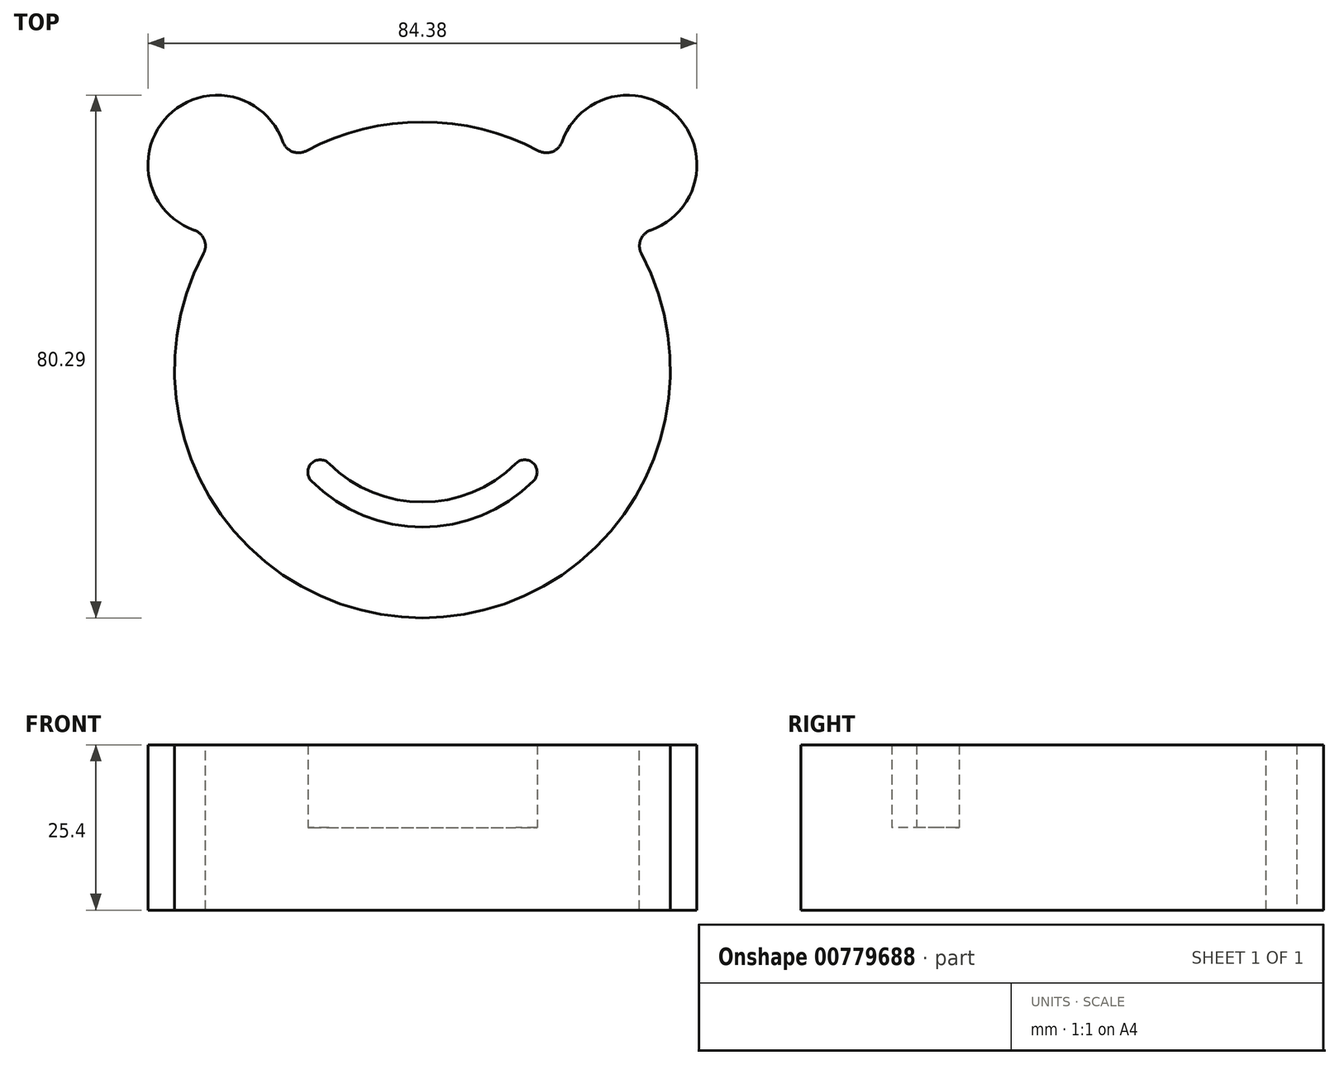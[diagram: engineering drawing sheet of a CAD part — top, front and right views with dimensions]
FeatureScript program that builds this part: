
annotation { "Feature Type Name" : "Feature", "Feature Type Description" : "" }
export const myFeature = defineFeature(function(context is Context, id is Id, definition is map)
    precondition{}
    {
        {
            var Q0;
            Q0=qCreatedBy(makeId("Top.planeOp"),FACE);
            var sketch = newSketch(context, id + "F0", { "sketchPlane" : qUnion([Q0])});
            skCircle(sketch, "E0", {"center": v(0, 0) * mm, "radius": 38.1 * mm});
            skCircle(sketch, "E1", {"center": v(0, 0) * mm, "radius": 31.75 * mm});
            skLineSegment(sketch, "E2", {"start": v(0, 31.75) * mm, "end": v(0, 55.25) * mm, "construction": true});
            skLineSegment(sketch, "E3", {"start": v(0, 55.25) * mm, "end": v(0, 44.58) * mm, "construction": true});
            skArc(sketch, "E4", {"start": v(7.8, 37.3) * mm, "mid": v(0, 55.25) * mm, "end": v(-7.8, 37.3) * mm});
            skArc(sketch, "E5.1.0", {"start": v(37.3, -7.8) * mm, "mid": v(55.25, 0) * mm, "end": v(37.3, 7.8) * mm});
            skLineSegment(sketch, "E5.anchor1", {"start": v(0, 0) * mm, "end": v(-7.8, 37.3) * mm, "construction": true});
            skLineSegment(sketch, "E5.anchor2", {"start": v(0, 0) * mm, "end": v(37.3, 7.8) * mm, "construction": true});
            skSolve(sketch);
        }
        {
            var Q0;
            Q0=qCreatedBy(makeId("Front.planeOp"),FACE);
            var sketch = newSketch(context, id + "F1", { "sketchPlane" : qUnion([Q0])});
            skLineSegment(sketch, "E6", {"start": v(0, 0) * mm, "end": v(0, 59.39) * mm, "construction": true});
            skSolve(sketch);
        }
        {
            var Q0;
            Q0 = qSketchRegion(id + "F0", true);
            var Q1;
            Q1=makeQuery(id+"F0.imprint","IMPRINT",FACE,{"disambiguationData":[TD([[makeQuery(id+"F0.imprint","IMPRINT",EDGE,{"derivedFrom":sQuery(id+"F0.wireOp",EDGE,"E1")}),1.0]])]});
            extrude(context, id + "F2", {"entities" : qUnion([Q0, Q1]), "depth" : 12.7 * mm, "offsetDistance" : 25.4 * mm});
        }
        {
            var Q0;
            Q0=makeQuery(id+"F2.opExtrude","CAP_FACE",FACE,{"disambiguationData":[OSD([sQuery(id+"F0.wireOp",EDGE,"E0"),sQuery(id+"F0.wireOp",EDGE,"E4"),sQuery(id+"F0.wireOp",EDGE,"E5.1.0")])],"isStart":false});
            var sketch = newSketch(context, id + "F3", { "sketchPlane" : qUnion([Q0])});
            skCircle(sketch, "E7", {"center": v(0, 20.32) * mm, "radius": 5.08 * mm});
            skCircle(sketch, "E8", {"center": v(20.32, 0) * mm, "radius": 5.08 * mm});
            skArc(sketch, "E9", {"start": v(0, -20.32) * mm, "mid": v(-14.37, -14.37) * mm, "end": v(-20.32, 0) * mm});
            skArc(sketch, "E10", {"start": v(0, -24.13) * mm, "mid": v(-17.06, -17.06) * mm, "end": v(-24.13, 0) * mm});
            skArc(sketch, "E11", {"start": v(-24.13, 0) * mm, "mid": v(-22.23, 1.9) * mm, "end": v(-20.32, 0) * mm});
            skArc(sketch, "E12", {"start": v(0, -24.13) * mm, "mid": v(1.9, -22.23) * mm, "end": v(0, -20.32) * mm});
            skSolve(sketch);
        }
        {
            var Q0;
            Q0=makeQuery(id+"F3.imprint","IMPRINT",FACE,{"disambiguationData":[TD([[makeQuery(id+"F3.imprint","IMPRINT",EDGE,{"derivedFrom":sQuery(id+"F3.wireOp",EDGE,"E7")}),1.0]])]});
            var Q1;
            Q1=makeQuery(id+"F3.imprint","IMPRINT",FACE,{"disambiguationData":[TD([[makeQuery(id+"F3.imprint","IMPRINT",EDGE,{"derivedFrom":sQuery(id+"F3.wireOp",EDGE,"E8")}),1.0]])]});
            var Q2;
            Q2=makeQuery(id+"F3.imprint","IMPRINT",FACE,{"disambiguationData":[TD([[makeQuery(id+"F3.imprint","IMPRINT",EDGE,{"derivedFrom":sQuery(id+"F3.wireOp",EDGE,"E9")}),1.0]])]});
            extrude(context, id + "F4", {"entities" : qUnion([Q0, Q1, Q2]), "operationType" : NewBodyOperationType.ADD, "depth" : 12.7 * mm, "offsetDistance" : 25.4 * mm});
        }
        {
            var Q0;
            Q0=makeQuery(id+"F0.imprint","IMPRINT",FACE,{"disambiguationData":[TD([[makeQuery(id+"F0.imprint","IMPRINT",EDGE,{"derivedFrom":sQuery(id+"F0.wireOp",EDGE,"E1")}),-1.0]])]});
            var Q1;
            {var subQ0=sQuery(id+"F0.wireOp",EDGE,"E4");Q1=makeQuery(id+"F0.imprint","IMPRINT",FACE,{"disambiguationData":[TD([[makeQuery(id+"F0.imprint","IMPRINT",EDGE,{"derivedFrom":subQ0}),1.0]])]});}
            var Q2;
            {var subQ0=sQuery(id+"F0.wireOp",EDGE,"E5.1.0");Q2=makeQuery(id+"F0.imprint","IMPRINT",FACE,{"disambiguationData":[TD([[makeQuery(id+"F0.imprint","IMPRINT",EDGE,{"derivedFrom":subQ0}),1.0]])]});}
            extrude(context, id + "F5", {"entities" : qUnion([Q0, Q1, Q2]), "operationType" : NewBodyOperationType.ADD, "depth" : 25.4 * mm, "offsetDistance" : 25.4 * mm});
        }
        {
            var Q0;
            Q0=makeQuery(id+"F2.opExtrude","SWEPT_BODY",BODY,{"disambiguationData":[OSD([sQuery(id+"F0.wireOp",EDGE,"E0"),sQuery(id+"F0.wireOp",EDGE,"E4"),sQuery(id+"F0.wireOp",EDGE,"E5.1.0")])]});
            var Q1;
            Q1=sQuery(id+"F1.wireOp",EDGE,"E6");
            transform(context, id + "F6", {"entities" : qUnion([Q0]), "transformType" : TransformType.ROTATION, "transformAxis" : qUnion([Q1]), "angle" : 45 * degree, "makeCopy" : false});
        }
        {
            var Q0;
            {var subQ0=sQuery(id+"F0.wireOp",EDGE,"E4");var subQ1=sQuery(id+"F0.wireOp",EDGE,"E0");var subQ2=makeQuery(id+"F0.imprint","INTERSECT",VERTEX,{"disambiguationData":[OD(0.0)],"derivedFrom":[subQ1,subQ0]});Q0=makeQuery(id+"F5.boolean.opBoolean","MERGE",EDGE,{"derivedFrom":[makeQuery(id+"F2.opExtrude","SWEPT_EDGE",EDGE,{"disambiguationData":[OSD([subQ1,subQ0]),TDD([subQ2])]}),makeQuery(id+"F5.opExtrude","SWEPT_EDGE",EDGE,{"disambiguationData":[OSD([subQ1,subQ0]),TDD([subQ2])]})]});}
            var Q1;
            {var subQ0=sQuery(id+"F0.wireOp",EDGE,"E4");var subQ1=sQuery(id+"F0.wireOp",EDGE,"E0");var subQ2=makeQuery(id+"F0.imprint","INTERSECT",VERTEX,{"disambiguationData":[OD(1.0)],"derivedFrom":[subQ1,subQ0]});Q1=makeQuery(id+"F5.boolean.opBoolean","MERGE",EDGE,{"derivedFrom":[makeQuery(id+"F2.opExtrude","SWEPT_EDGE",EDGE,{"disambiguationData":[OSD([subQ1,subQ0]),TDD([subQ2])]}),makeQuery(id+"F5.opExtrude","SWEPT_EDGE",EDGE,{"disambiguationData":[OSD([subQ1,subQ0]),TDD([subQ2])]})]});}
            var Q2;
            {var subQ0=sQuery(id+"F0.wireOp",EDGE,"E5.1.0");var subQ1=sQuery(id+"F0.wireOp",EDGE,"E0");var subQ2=makeQuery(id+"F0.imprint","INTERSECT",VERTEX,{"disambiguationData":[OD(1.0)],"derivedFrom":[subQ1,subQ0]});Q2=makeQuery(id+"F5.boolean.opBoolean","MERGE",EDGE,{"derivedFrom":[makeQuery(id+"F2.opExtrude","SWEPT_EDGE",EDGE,{"disambiguationData":[OSD([subQ1,subQ0]),TDD([subQ2])]}),makeQuery(id+"F5.opExtrude","SWEPT_EDGE",EDGE,{"disambiguationData":[OSD([subQ1,subQ0]),TDD([subQ2])]})]});}
            var Q3;
            {var subQ0=sQuery(id+"F0.wireOp",EDGE,"E5.1.0");var subQ1=sQuery(id+"F0.wireOp",EDGE,"E0");var subQ2=makeQuery(id+"F0.imprint","INTERSECT",VERTEX,{"disambiguationData":[OD(0.0)],"derivedFrom":[subQ1,subQ0]});Q3=makeQuery(id+"F5.boolean.opBoolean","MERGE",EDGE,{"derivedFrom":[makeQuery(id+"F2.opExtrude","SWEPT_EDGE",EDGE,{"disambiguationData":[OSD([subQ1,subQ0]),TDD([subQ2])]}),makeQuery(id+"F5.opExtrude","SWEPT_EDGE",EDGE,{"disambiguationData":[OSD([subQ1,subQ0]),TDD([subQ2])]})]});}
            fillet(context, id + "F7", {"entities" : qUnion([Q0, Q1, Q2, Q3]), "radius" : 2.54 * mm, "tangentPropagation" : true, "allowEdgeOverflow" : false});
        }
    });
